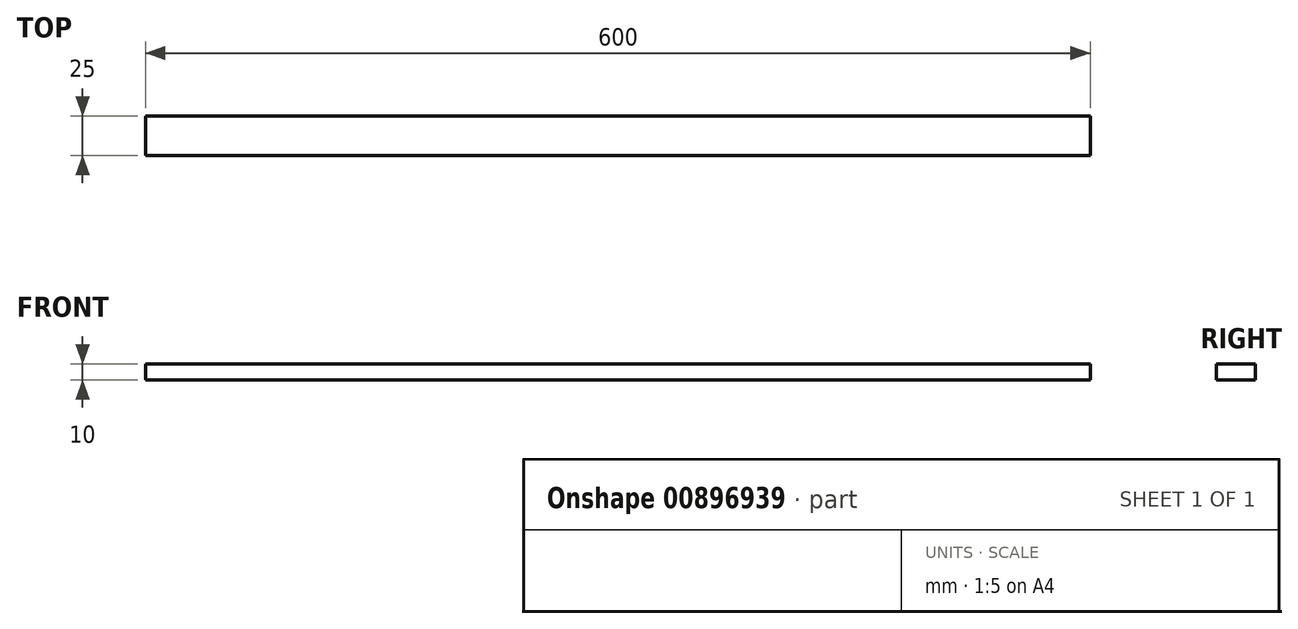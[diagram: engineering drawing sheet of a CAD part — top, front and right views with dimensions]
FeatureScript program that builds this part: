
annotation { "Feature Type Name" : "Feature", "Feature Type Description" : "" }
export const myFeature = defineFeature(function(context is Context, id is Id, definition is map)
    precondition{}
    {
        {
            var Q0;
            Q0=qCreatedBy(makeId("Front.planeOp"),FACE);
            var sketch = newSketch(context, id + "F0", { "sketchPlane" : qUnion([Q0])});
            skLineSegment(sketch, "E0.bottom", {"start": v(300, 5) * mm, "end": v(-300, 5) * mm});
            skLineSegment(sketch, "E0.top", {"start": v(300, -5) * mm, "end": v(-300, -5) * mm});
            skLineSegment(sketch, "E0.left", {"start": v(300, 5) * mm, "end": v(300, -5) * mm});
            skLineSegment(sketch, "E0.right", {"start": v(-300, 5) * mm, "end": v(-300, -5) * mm});
            skPoint(sketch, "E0.middle", {"position": v(0, 0) * mm});
            skSolve(sketch);
        }
        {
            var Q0;
            Q0 = qSketchRegion(id + "F0", true);
            extrude(context, id + "F1", {"entities" : qUnion([Q0]), "depth" : 25 * mm, "offsetDistance" : 25 * mm});
        }
    });
